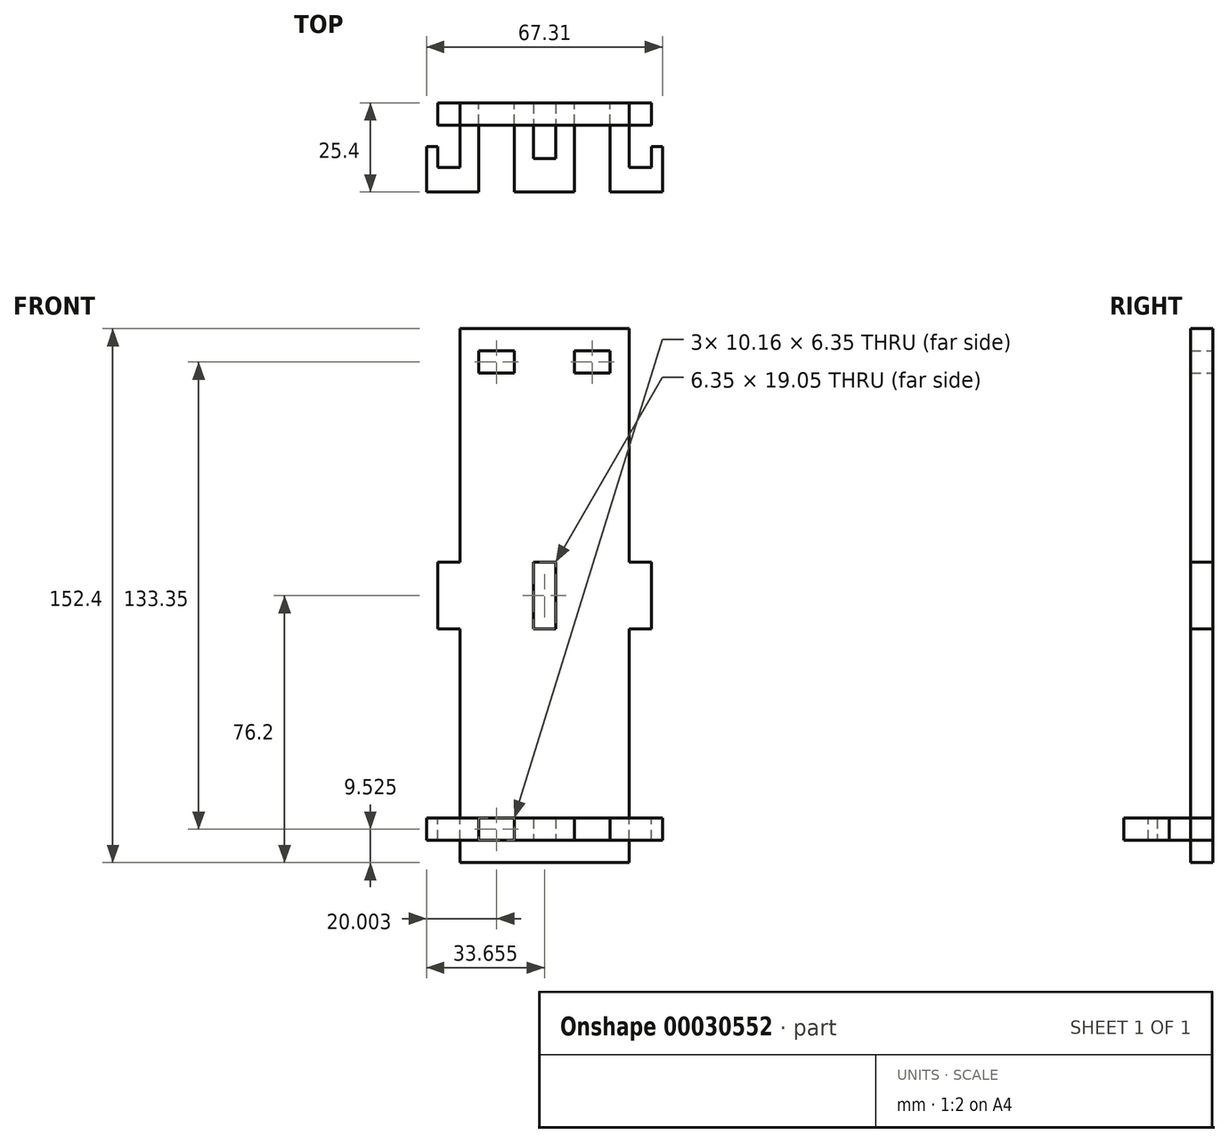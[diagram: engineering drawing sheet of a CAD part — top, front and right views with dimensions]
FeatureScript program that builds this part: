
annotation { "Feature Type Name" : "Feature", "Feature Type Description" : "" }
export const myFeature = defineFeature(function(context is Context, id is Id, definition is map)
    precondition{}
    {
        {
            var Q0;
            Q0=qCreatedBy(makeId("Top.planeOp"),FACE);
            var sketch = newSketch(context, id + "F0", { "sketchPlane" : qUnion([Q0])});
            skLineSegment(sketch, "E0.bottom", {"start": v(0, 0) * mm, "end": v(14.92, 0) * mm});
            skLineSegment(sketch, "E0.top", {"start": v(0, 19.05) * mm, "end": v(14.92, 19.05) * mm});
            skLineSegment(sketch, "E0.left", {"start": v(0, 0) * mm, "end": v(0, 19.05) * mm});
            skLineSegment(sketch, "E0.right", {"start": v(67.31, 0) * mm, "end": v(67.31, 19.05) * mm});
            skLineSegment(sketch, "E1", {"start": v(14.92, 0) * mm, "end": v(14.92, 2.54) * mm});
            skArc(sketch, "E2", {"start": v(25.08, 2.54) * mm, "mid": v(20, 7.62) * mm, "end": v(14.92, 2.54) * mm});
            skLineSegment(sketch, "E3", {"start": v(25.08, 2.54) * mm, "end": v(25.08, 0) * mm});
            skLineSegment(sketch, "E4.trimOffspring", {"start": v(25.08, 0) * mm, "end": v(42.23, 0) * mm});
            skLineSegment(sketch, "E5", {"start": v(33.66, 19.05) * mm, "end": v(33.66, 0) * mm, "construction": true});
            skLineSegment(sketch, "E6", {"start": v(30.48, 19.05) * mm, "end": v(30.48, 9.53) * mm});
            skLineSegment(sketch, "E7", {"start": v(30.48, 9.53) * mm, "end": v(36.83, 9.53) * mm});
            skLineSegment(sketch, "E8", {"start": v(36.83, 9.53) * mm, "end": v(36.83, 19.05) * mm});
            skLineSegment(sketch, "E9.MirrorCS", {"start": v(42.23, 2.54) * mm, "end": v(42.23, 0) * mm});
            skArc(sketch, "E10.MirrorCS", {"start": v(42.23, 2.54) * mm, "mid": v(47.3, 7.62) * mm, "end": v(52.39, 2.54) * mm});
            skLineSegment(sketch, "E11.MirrorCS", {"start": v(52.39, 0) * mm, "end": v(52.39, 2.54) * mm});
            skLineSegment(sketch, "E12.trimOffspring", {"start": v(52.39, 0) * mm, "end": v(67.31, 0) * mm});
            skLineSegment(sketch, "E13.trimOffspring", {"start": v(36.83, 19.05) * mm, "end": v(42.23, 19.05) * mm});
            skLineSegment(sketch, "E14.top", {"start": v(14.92, 25.4) * mm, "end": v(25.08, 25.4) * mm});
            skLineSegment(sketch, "E14.left", {"start": v(14.92, 19.05) * mm, "end": v(14.92, 25.4) * mm});
            skLineSegment(sketch, "E14.right", {"start": v(25.08, 19.05) * mm, "end": v(25.08, 25.4) * mm});
            skLineSegment(sketch, "E15.top", {"start": v(42.23, 25.4) * mm, "end": v(52.39, 25.4) * mm});
            skLineSegment(sketch, "E15.left", {"start": v(42.23, 19.05) * mm, "end": v(42.23, 25.4) * mm});
            skLineSegment(sketch, "E15.right", {"start": v(52.39, 19.05) * mm, "end": v(52.39, 25.4) * mm});
            skLineSegment(sketch, "E16.trimOffspring", {"start": v(25.08, 19.05) * mm, "end": v(30.48, 19.05) * mm});
            skLineSegment(sketch, "E17.trimOffspring", {"start": v(52.39, 19.05) * mm, "end": v(67.31, 19.05) * mm});
            skLineSegment(sketch, "E18.bottom", {"start": v(30.48, 19.05) * mm, "end": v(9.53, 19.05) * mm, "construction": true});
            skLineSegment(sketch, "E18.top", {"start": v(30.48, 0) * mm, "end": v(9.53, 0) * mm, "construction": true});
            skLineSegment(sketch, "E18.left", {"start": v(30.48, 19.05) * mm, "end": v(30.48, 0) * mm, "construction": true});
            skLineSegment(sketch, "E18.right", {"start": v(9.53, 19.05) * mm, "end": v(9.53, 0) * mm, "construction": true});
            skLineSegment(sketch, "E19.bottom", {"start": v(36.83, 19.05) * mm, "end": v(57.79, 19.05) * mm, "construction": true});
            skLineSegment(sketch, "E19.top", {"start": v(36.83, 0) * mm, "end": v(57.79, 0) * mm, "construction": true});
            skLineSegment(sketch, "E19.left", {"start": v(36.83, 19.05) * mm, "end": v(36.83, 0) * mm, "construction": true});
            skLineSegment(sketch, "E19.right", {"start": v(57.79, 19.05) * mm, "end": v(57.79, 0) * mm, "construction": true});
            skLineSegment(sketch, "E20", {"start": v(20, 0) * mm, "end": v(20, 2.54) * mm, "construction": true});
            skLineSegment(sketch, "E21", {"start": v(47.3, 0) * mm, "end": v(47.3, 2.54) * mm, "construction": true});
            skSolve(sketch);
        }
        {
            var Q0;
            Q0=makeQuery(id+"F0.imprint","IMPRINT",FACE,{"disambiguationData":[TD([[makeQuery(id+"F0.imprint","IMPRINT",EDGE,{"derivedFrom":sQuery(id+"F0.wireOp",EDGE,"E0.bottom")}),1.0]])]});
            extrude(context, id + "F1", {"entities" : qUnion([Q0]), "depth" : 6.35 * mm});
        }
        {
            var Q0;
            Q0=makeQuery(id+"F1.opExtrude","CAP_FACE",FACE,{"disambiguationData":[OSD([sQuery(id+"F0.wireOp",EDGE,"E0.bottom"),sQuery(id+"F0.wireOp",EDGE,"E0.top"),sQuery(id+"F0.wireOp",EDGE,"E0.left"),sQuery(id+"F0.wireOp",EDGE,"E0.right"),sQuery(id+"F0.wireOp",EDGE,"E1"),sQuery(id+"F0.wireOp",EDGE,"E2"),sQuery(id+"F0.wireOp",EDGE,"E3"),sQuery(id+"F0.wireOp",EDGE,"E4.trimOffspring"),sQuery(id+"F0.wireOp",EDGE,"E6"),sQuery(id+"F0.wireOp",EDGE,"E7"),sQuery(id+"F0.wireOp",EDGE,"E8"),sQuery(id+"F0.wireOp",EDGE,"E9.MirrorCS"),sQuery(id+"F0.wireOp",EDGE,"E10.MirrorCS"),sQuery(id+"F0.wireOp",EDGE,"E11.MirrorCS"),sQuery(id+"F0.wireOp",EDGE,"E12.trimOffspring"),sQuery(id+"F0.wireOp",EDGE,"E13.trimOffspring"),sQuery(id+"F0.wireOp",EDGE,"E14.top"),sQuery(id+"F0.wireOp",EDGE,"E14.left"),sQuery(id+"F0.wireOp",EDGE,"E14.right"),sQuery(id+"F0.wireOp",EDGE,"E15.top"),sQuery(id+"F0.wireOp",EDGE,"E15.left"),sQuery(id+"F0.wireOp",EDGE,"E15.right"),sQuery(id+"F0.wireOp",EDGE,"E16.trimOffspring"),sQuery(id+"F0.wireOp",EDGE,"E17.trimOffspring")])],"isStart":false});
            var sketch = newSketch(context, id + "F2", { "sketchPlane" : qUnion([Q0])});
            skLineSegment(sketch, "E22.bottom", {"start": v(3.18, 19.05) * mm, "end": v(9.52, 19.05) * mm});
            skLineSegment(sketch, "E22.top", {"start": v(3.18, 6.99) * mm, "end": v(9.52, 6.99) * mm});
            skLineSegment(sketch, "E22.left", {"start": v(3.17, 19.05) * mm, "end": v(3.18, 6.99) * mm});
            skLineSegment(sketch, "E22.right", {"start": v(9.52, 19.05) * mm, "end": v(9.52, 6.99) * mm});
            skLineSegment(sketch, "E23.bottom", {"start": v(64.14, 19.05) * mm, "end": v(57.79, 19.05) * mm});
            skLineSegment(sketch, "E23.top", {"start": v(64.14, 6.99) * mm, "end": v(57.79, 6.99) * mm});
            skLineSegment(sketch, "E23.left", {"start": v(64.14, 19.05) * mm, "end": v(64.14, 6.99) * mm});
            skLineSegment(sketch, "E23.right", {"start": v(57.79, 19.05) * mm, "end": v(57.79, 6.99) * mm});
            skLineSegment(sketch, "E24.bottom", {"start": v(0, 19.05) * mm, "end": v(3.18, 19.05) * mm});
            skLineSegment(sketch, "E24.top", {"start": v(0, 13.02) * mm, "end": v(3.18, 13.02) * mm});
            skLineSegment(sketch, "E24.left", {"start": v(0, 19.05) * mm, "end": v(0, 13.02) * mm});
            skLineSegment(sketch, "E24.right", {"start": v(3.17, 19.05) * mm, "end": v(3.17, 13.02) * mm});
            skLineSegment(sketch, "E25.bottom", {"start": v(67.31, 19.05) * mm, "end": v(64.14, 19.05) * mm});
            skLineSegment(sketch, "E25.top", {"start": v(67.31, 13.02) * mm, "end": v(64.14, 13.02) * mm});
            skLineSegment(sketch, "E25.left", {"start": v(67.31, 19.05) * mm, "end": v(67.31, 13.02) * mm});
            skLineSegment(sketch, "E25.right", {"start": v(64.14, 19.05) * mm, "end": v(64.14, 13.02) * mm});
            skSolve(sketch);
        }
        {
            var Q0;
            Q0=makeQuery(id+"F2.imprint","IMPRINT",FACE,{"disambiguationData":[TD([[makeQuery(id+"F2.imprint","IMPRINT",EDGE,{"derivedFrom":sQuery(id+"F2.wireOp",EDGE,"E24.bottom")}),-1.0]])]});
            var Q1;
            Q1=makeQuery(id+"F2.imprint","IMPRINT",FACE,{"disambiguationData":[TD([[makeQuery(id+"F2.imprint","IMPRINT",EDGE,{"derivedFrom":sQuery(id+"F2.wireOp",EDGE,"E22.bottom")}),-1.0]])]});
            var Q2;
            Q2=makeQuery(id+"F2.imprint","IMPRINT",FACE,{"disambiguationData":[TD([[makeQuery(id+"F2.imprint","IMPRINT",EDGE,{"derivedFrom":sQuery(id+"F2.wireOp",EDGE,"E23.bottom")}),-1.0]])]});
            var Q3;
            Q3=makeQuery(id+"F2.imprint","IMPRINT",FACE,{"disambiguationData":[TD([[makeQuery(id+"F2.imprint","IMPRINT",EDGE,{"derivedFrom":sQuery(id+"F2.wireOp",EDGE,"E25.bottom")}),-1.0]])]});
            extrude(context, id + "F3", {"entities" : qUnion([Q0, Q1, Q2, Q3]), "operationType" : NewBodyOperationType.REMOVE, "endBound" : BoundingType.THROUGH_ALL, "oppositeDirection" : true, "depth" : 25.4 * mm});
        }
        {
            var Q0;
            Q0=makeQuery(id+"F1.opExtrude","SWEPT_FACE",FACE,{"disambiguationData":[OSD([sQuery(id+"F0.wireOp",EDGE,"E17.trimOffspring")])]});
            var sketch = newSketch(context, id + "F4", { "sketchPlane" : qUnion([Q0])});
            skLineSegment(sketch, "E26.bottom", {"start": v(-57.79, -6.35) * mm, "end": v(-9.52, -6.35) * mm});
            skLineSegment(sketch, "E26.top", {"start": v(-57.79, 146.05) * mm, "end": v(-9.53, 146.05) * mm});
            skLineSegment(sketch, "E26.left", {"start": v(-57.79, -6.35) * mm, "end": v(-57.79, 146.05) * mm});
            skLineSegment(sketch, "E26.right", {"start": v(-9.52, -6.35) * mm, "end": v(-9.53, 146.05) * mm});
            skLineSegment(sketch, "E27.0", {"start": v(-57.79, 0) * mm, "end": v(-57.79, 6.35) * mm});
            skLineSegment(sketch, "E28.0", {"start": v(-9.52, 0) * mm, "end": v(-9.52, 6.35) * mm});
            skSolve(sketch);
        }
        {
            var Q0;
            {var subQ6=sQuery(id+"F4.wireOp",EDGE,"E26.bottom");Q0=makeQuery(id+"F4.imprint","IMPRINT",FACE,{"disambiguationData":[TD([[makeQuery(id+"F4.imprint","IMPRINT",EDGE,{"derivedFrom":subQ6}),1.0]])]});}
            var Q1;
            Q1=makeQuery(id+"F4.imprint","IMPRINT",FACE,{"disambiguationData":[TD([[makeQuery(id+"F4.imprint","IMPRINT",EDGE,{"derivedFrom":sQuery(id+"F4.wireOp",EDGE,"E27.0")}),-1.0]])]});
            extrude(context, id + "F5", {"entities" : qUnion([Q0, Q1]), "depth" : 6.35 * mm});
        }
        {
            var Q0;
            Q0=makeQuery(id+"F5.opExtrude","CAP_FACE",FACE,{"disambiguationData":[OSD([sQuery(id+"F4.wireOp",EDGE,"E26.bottom"),sQuery(id+"F4.wireOp",EDGE,"E26.top"),sQuery(id+"F4.wireOp",EDGE,"E26.left"),sQuery(id+"F4.wireOp",EDGE,"E26.right"),sQuery(id+"F4.wireOp",EDGE,"E27.0"),sQuery(id+"F4.wireOp",EDGE,"E28.0")])],"isStart":false});
            var sketch = newSketch(context, id + "F6", { "sketchPlane" : qUnion([Q0])});
            skLineSegment(sketch, "E29.0.0", {"start": v(-52.39, 0) * mm, "end": v(-42.23, 0) * mm});
            skLineSegment(sketch, "E29.0.1", {"start": v(-42.23, 0) * mm, "end": v(-42.23, 6.35) * mm});
            skLineSegment(sketch, "E29.0.2", {"start": v(-42.23, 6.35) * mm, "end": v(-52.39, 6.35) * mm});
            skLineSegment(sketch, "E29.0.3", {"start": v(-52.39, 6.35) * mm, "end": v(-52.39, 0) * mm});
            skLineSegment(sketch, "E30.0.0", {"start": v(-25.08, 0) * mm, "end": v(-14.92, 0) * mm});
            skLineSegment(sketch, "E30.0.1", {"start": v(-14.92, 0) * mm, "end": v(-14.92, 6.35) * mm});
            skLineSegment(sketch, "E30.0.2", {"start": v(-14.92, 6.35) * mm, "end": v(-25.08, 6.35) * mm});
            skLineSegment(sketch, "E30.0.3", {"start": v(-25.08, 6.35) * mm, "end": v(-25.08, 0) * mm});
            skSolve(sketch);
        }
        {
            var Q0;
            Q0=makeQuery(id+"F6.imprint","IMPRINT",FACE,{"disambiguationData":[TD([[makeQuery(id+"F6.imprint","IMPRINT",EDGE,{"derivedFrom":sQuery(id+"F6.wireOp",EDGE,"E29.0.0")}),1.0]])]});
            var Q1;
            Q1=makeQuery(id+"F6.imprint","IMPRINT",FACE,{"disambiguationData":[TD([[makeQuery(id+"F6.imprint","IMPRINT",EDGE,{"derivedFrom":sQuery(id+"F6.wireOp",EDGE,"E30.0.0")}),1.0]])]});
            extrude(context, id + "F7", {"entities" : qUnion([Q0, Q1]), "operationType" : NewBodyOperationType.REMOVE, "endBound" : BoundingType.THROUGH_ALL, "oppositeDirection" : true, "depth" : 25.4 * mm});
        }
        {
            var Q0;
            {var subQ6=sQuery(id+"F4.wireOp",EDGE,"E26.bottom");Q0=makeQuery(id+"F4.imprint","IMPRINT",FACE,{"disambiguationData":[TD([[makeQuery(id+"F4.imprint","IMPRINT",EDGE,{"derivedFrom":subQ6}),1.0]])]});}
            var sketch = newSketch(context, id + "F8", { "sketchPlane" : qUnion([Q0])});
            skLineSegment(sketch, "E31.0", {"start": v(-57.79, -6.35) * mm, "end": v(-57.79, 146.05) * mm});
            skLineSegment(sketch, "E32.0", {"start": v(-9.52, -6.35) * mm, "end": v(-9.53, 146.05) * mm});
            skLineSegment(sketch, "E33.rect.bottom", {"start": v(-64.14, 79.38) * mm, "end": v(-51.44, 79.38) * mm});
            skLineSegment(sketch, "E33.rect.top", {"start": v(-64.14, 60.32) * mm, "end": v(-51.44, 60.32) * mm});
            skLineSegment(sketch, "E33.rect.left", {"start": v(-64.14, 79.38) * mm, "end": v(-64.14, 60.32) * mm});
            skLineSegment(sketch, "E33.rect.right", {"start": v(-51.44, 79.38) * mm, "end": v(-51.44, 60.33) * mm});
            skPoint(sketch, "E33.rect.middle", {"position": v(-57.79, 69.85) * mm});
            skLineSegment(sketch, "E34.rect.bottom", {"start": v(-3.18, 79.38) * mm, "end": v(-15.88, 79.38) * mm});
            skLineSegment(sketch, "E34.rect.top", {"start": v(-3.18, 60.33) * mm, "end": v(-15.87, 60.33) * mm});
            skLineSegment(sketch, "E34.rect.left", {"start": v(-3.18, 79.38) * mm, "end": v(-3.18, 60.33) * mm});
            skLineSegment(sketch, "E34.rect.right", {"start": v(-15.87, 79.38) * mm, "end": v(-15.87, 60.33) * mm});
            skPoint(sketch, "E34.rect.middle", {"position": v(-9.53, 69.85) * mm});
            skSolve(sketch);
        }
        {
            var Q0;
            {var subQ0=sQuery(id+"F8.wireOp",EDGE,"E34.rect.left");Q0=makeQuery(id+"F8.imprint","IMPRINT",FACE,{"disambiguationData":[TD([[makeQuery(id+"F8.imprint","IMPRINT",EDGE,{"derivedFrom":subQ0}),-1.0]])]});}
            var Q1;
            {var subQ0=sQuery(id+"F8.wireOp",EDGE,"E33.rect.left");Q1=makeQuery(id+"F8.imprint","IMPRINT",FACE,{"disambiguationData":[TD([[makeQuery(id+"F8.imprint","IMPRINT",EDGE,{"derivedFrom":subQ0}),1.0]])]});}
            var Q2;
            Q2=makeQuery(id+"F5.opExtrude","CAP_FACE",FACE,{"disambiguationData":[OSD([sQuery(id+"F4.wireOp",EDGE,"E26.bottom"),sQuery(id+"F4.wireOp",EDGE,"E26.top"),sQuery(id+"F4.wireOp",EDGE,"E26.left"),sQuery(id+"F4.wireOp",EDGE,"E26.right"),sQuery(id+"F4.wireOp",EDGE,"E27.0"),sQuery(id+"F4.wireOp",EDGE,"E28.0")])],"isStart":false});
            extrude(context, id + "F9", {"entities" : qUnion([Q0, Q1]), "operationType" : NewBodyOperationType.ADD, "endBound" : BoundingType.UP_TO_SURFACE, "endBoundEntityFace" : qUnion([Q2]), "depth" : 25.4 * mm});
        }
        {
            var Q0;
            Q0=makeQuery(id+"F9.boolean.opBoolean","MERGE",FACE,{"derivedFrom":[makeQuery(id+"F5.opExtrude","CAP_FACE",FACE,{"disambiguationData":[OSD([sQuery(id+"F4.wireOp",EDGE,"E26.bottom"),sQuery(id+"F4.wireOp",EDGE,"E26.top"),sQuery(id+"F4.wireOp",EDGE,"E26.left"),sQuery(id+"F4.wireOp",EDGE,"E26.right"),sQuery(id+"F4.wireOp",EDGE,"E27.0"),sQuery(id+"F4.wireOp",EDGE,"E28.0")])],"isStart":false}),makeQuery(id+"F9.opExtrude","CAP_FACE",FACE,{"disambiguationData":[OSD([sQuery(id+"F8.wireOp",EDGE,"E31.0"),sQuery(id+"F8.wireOp",EDGE,"E33.rect.bottom"),sQuery(id+"F8.wireOp",EDGE,"E33.rect.top"),sQuery(id+"F8.wireOp",EDGE,"E33.rect.left")])],"isStart":false}),makeQuery(id+"F9.opExtrude","CAP_FACE",FACE,{"disambiguationData":[OSD([sQuery(id+"F8.wireOp",EDGE,"E32.0"),sQuery(id+"F8.wireOp",EDGE,"E34.rect.bottom"),sQuery(id+"F8.wireOp",EDGE,"E34.rect.top"),sQuery(id+"F8.wireOp",EDGE,"E34.rect.left")])],"isStart":false})]});
            var sketch = newSketch(context, id + "F10", { "sketchPlane" : qUnion([Q0])});
            skLineSegment(sketch, "E35.2", {"start": v(-9.52, -6.35) * mm, "end": v(-9.53, 146.05) * mm});
            skLineSegment(sketch, "E35.3", {"start": v(-57.79, -6.35) * mm, "end": v(-57.79, 146.05) * mm});
            skLineSegment(sketch, "E36", {"start": v(-57.79, 69.85) * mm, "end": v(-9.53, 69.85) * mm, "construction": true});
            skLineSegment(sketch, "E37.0.0", {"start": v(-52.39, 0) * mm, "end": v(-42.23, 0) * mm});
            skLineSegment(sketch, "E37.0.1", {"start": v(-42.23, 0) * mm, "end": v(-42.23, 6.35) * mm});
            skLineSegment(sketch, "E37.0.2", {"start": v(-42.23, 6.35) * mm, "end": v(-52.39, 6.35) * mm});
            skLineSegment(sketch, "E37.0.3", {"start": v(-52.39, 6.35) * mm, "end": v(-52.39, 0) * mm});
            skLineSegment(sketch, "E38.0.0", {"start": v(-25.08, 0) * mm, "end": v(-14.92, 0) * mm});
            skLineSegment(sketch, "E38.0.1", {"start": v(-14.92, 0) * mm, "end": v(-14.92, 6.35) * mm});
            skLineSegment(sketch, "E38.0.2", {"start": v(-14.92, 6.35) * mm, "end": v(-25.08, 6.35) * mm});
            skLineSegment(sketch, "E38.0.3", {"start": v(-25.08, 6.35) * mm, "end": v(-25.08, 0) * mm});
            skLineSegment(sketch, "E39.MirrorCS", {"start": v(-52.39, 139.7) * mm, "end": v(-42.23, 139.7) * mm});
            skLineSegment(sketch, "E40.MirrorCS", {"start": v(-42.23, 139.7) * mm, "end": v(-42.23, 133.35) * mm});
            skLineSegment(sketch, "E41.MirrorCS", {"start": v(-42.23, 133.35) * mm, "end": v(-52.39, 133.35) * mm});
            skLineSegment(sketch, "E42.MirrorCS", {"start": v(-52.39, 133.35) * mm, "end": v(-52.39, 139.7) * mm});
            skLineSegment(sketch, "E43.MirrorCS", {"start": v(-25.08, 133.35) * mm, "end": v(-25.08, 139.7) * mm});
            skLineSegment(sketch, "E44.MirrorCS", {"start": v(-14.92, 133.35) * mm, "end": v(-25.08, 133.35) * mm});
            skLineSegment(sketch, "E45.MirrorCS", {"start": v(-14.92, 139.7) * mm, "end": v(-14.92, 133.35) * mm});
            skLineSegment(sketch, "E46.MirrorCS", {"start": v(-25.08, 139.7) * mm, "end": v(-14.92, 139.7) * mm});
            skSolve(sketch);
        }
        {
            var Q0;
            Q0=makeQuery(id+"F10.imprint","IMPRINT",FACE,{"disambiguationData":[TD([[makeQuery(id+"F10.imprint","IMPRINT",EDGE,{"derivedFrom":sQuery(id+"F10.wireOp",EDGE,"E39.MirrorCS")}),-1.0]])]});
            var Q1;
            Q1=makeQuery(id+"F10.imprint","IMPRINT",FACE,{"disambiguationData":[TD([[makeQuery(id+"F10.imprint","IMPRINT",EDGE,{"derivedFrom":sQuery(id+"F10.wireOp",EDGE,"E43.MirrorCS")}),-1.0]])]});
            extrude(context, id + "F11", {"entities" : qUnion([Q0, Q1]), "operationType" : NewBodyOperationType.REMOVE, "endBound" : BoundingType.THROUGH_ALL, "oppositeDirection" : true, "depth" : 25.4 * mm});
        }
        {
            var Q0;
            {var subQ6=sQuery(id+"F4.wireOp",EDGE,"E26.bottom");Q0=makeQuery(id+"F4.imprint","IMPRINT",FACE,{"disambiguationData":[TD([[makeQuery(id+"F4.imprint","IMPRINT",EDGE,{"derivedFrom":subQ6}),1.0]])]});}
            var sketch = newSketch(context, id + "F12", { "sketchPlane" : qUnion([Q0])});
            skLineSegment(sketch, "E47.bottom", {"start": v(-30.48, 60.33) * mm, "end": v(-36.83, 60.33) * mm});
            skLineSegment(sketch, "E47.top", {"start": v(-30.48, 79.38) * mm, "end": v(-36.83, 79.38) * mm});
            skLineSegment(sketch, "E47.left", {"start": v(-30.48, 60.33) * mm, "end": v(-30.48, 79.38) * mm});
            skLineSegment(sketch, "E47.right", {"start": v(-36.83, 60.33) * mm, "end": v(-36.83, 79.38) * mm});
            skLineSegment(sketch, "E48.0", {"start": v(-57.79, 146.05) * mm, "end": v(-9.53, 146.05) * mm});
            skLineSegment(sketch, "E49", {"start": v(-33.66, 146.05) * mm, "end": v(-33.66, 79.38) * mm, "construction": true});
            skSolve(sketch);
        }
        {
            var Q0;
            Q0 = qSketchRegion(id + "F12", true);
            extrude(context, id + "F13", {"entities" : qUnion([Q0]), "operationType" : NewBodyOperationType.REMOVE, "endBound" : BoundingType.THROUGH_ALL, "depth" : 25.4 * mm});
        }
    });
